# Revit family: Hager-Typ.B_TP&N_125A_Side_Extension_Boxes-empty-UK-en
name_source: partatom
category: Electrical Equipment
units: mm (PartAtom-declared; Revit-internal decimal feet)

## family parameters
Cut with Voids When Loaded = No
Host = Face
Panel Configuration = Two Columns, Circuits Across
Part Type = Panelboard
Room Calculation Point = No
Round Connector Dimension = Use Diameter
Shared = No

## types (5) — shared parameters
EF000003 - Mounting method = EV000384 - Surface mounted (plaster)
EF000007 - Colour = EV000154 - Other
EF000008 - Width = 465 mm  [stored 1.52559 ft]
EF000049 - Depth = 92 mm  [stored 0.301837 ft]
EF000118 - With mounting plate = No
EF000339 - Type of cover = EV004216 - Door
EF001062 - EMC-version = No
EF001088 - Extension possible = No
EF001134 - DIN-rail = No
EF001596 - Material housing = EV000179 - Steel
EF004462 - Type of closure = EV000154 - Other
EF006244 - Transparent cover/door = No
EF006306 - With lock = No
EF015776 - Earthing terminal block = Yes
EF015777 - Neutral terminal block = Yes
EF015941 - Signal passing door = No
HG000002 - With door or cover = Yes
HG000003 - Range = Type B TP&N Distribution Boards
HG000005 - Thickness = 3 mm  [stored 0.00984252 ft]
HG000006 - Flush mounted = No
HG000009 - Double swing door = No
HG000010 - Asymmetric doors = No
HG000011 - Empty rows from bottom = No
HG000017 - Distance between poles = 18 mm  [stored 0.0590551 ft]
Manufacturer = Hager
Type Comments = Type B TP&N Distribution Boards
zero-valued in all types: Default Elevation, EF000218 - Built-in depth, EF000266 - Number of rows, EF000332 - Built-in height, EF000846 - Built-in width, EF001131 - Internal depth, EF002950 - Width in number of modular spacings, HG000001 - Number of columns, HG000007 - Number of empty columns, HG000008 - Number of empty rows

## per-type parameters (varying)
| type | EF000040 - Height | EF005474 - Degree of protection (IP) | HG000004 - Manufacturer reference | Model |
| Surface mounted IP30 W465 H950 D91.5 0 Modular spacings - JK116BSF | 950 mm  [stored 3.1168 ft] | EV006410 - IP30 | JK116BSF | JK116BSF |
| Surface mounted P2XC W465 H500 D91.5 0 Modular spacings - JK104BSF | 500 mm  [stored 1.64042 ft] | EV009848 - IP2XC | JK104BSF | JK104BSF |
| Surface mounted P2XC W465 H550 D91.5 0 Modular spacings - JK106BSF | 550 mm | EV009848 - IP2XC | JK106BSF | JK106BSF |
| Surface mounted P2XC W465 H625 D91.5 0 Modular spacings - JK108BSF | 625 mm  [stored 2.05052 ft] | EV009848 - IP2XC | JK108BSF | JK108BSF |
| Surface mounted P2XC W465 H850 D91.5 0 Modular spacings - JK112BSF | 850 mm  [stored 2.78871 ft] | EV009848 - IP2XC | JK112BSF | JK112BSF |

note: [stored X ft] marks values corroborated as IEEE doubles in the binary element streams (Revit-internal decimal feet)

## geometry (parser evidence)
native form markers: Sweep x17
no freeform markers — native parametric forms only
